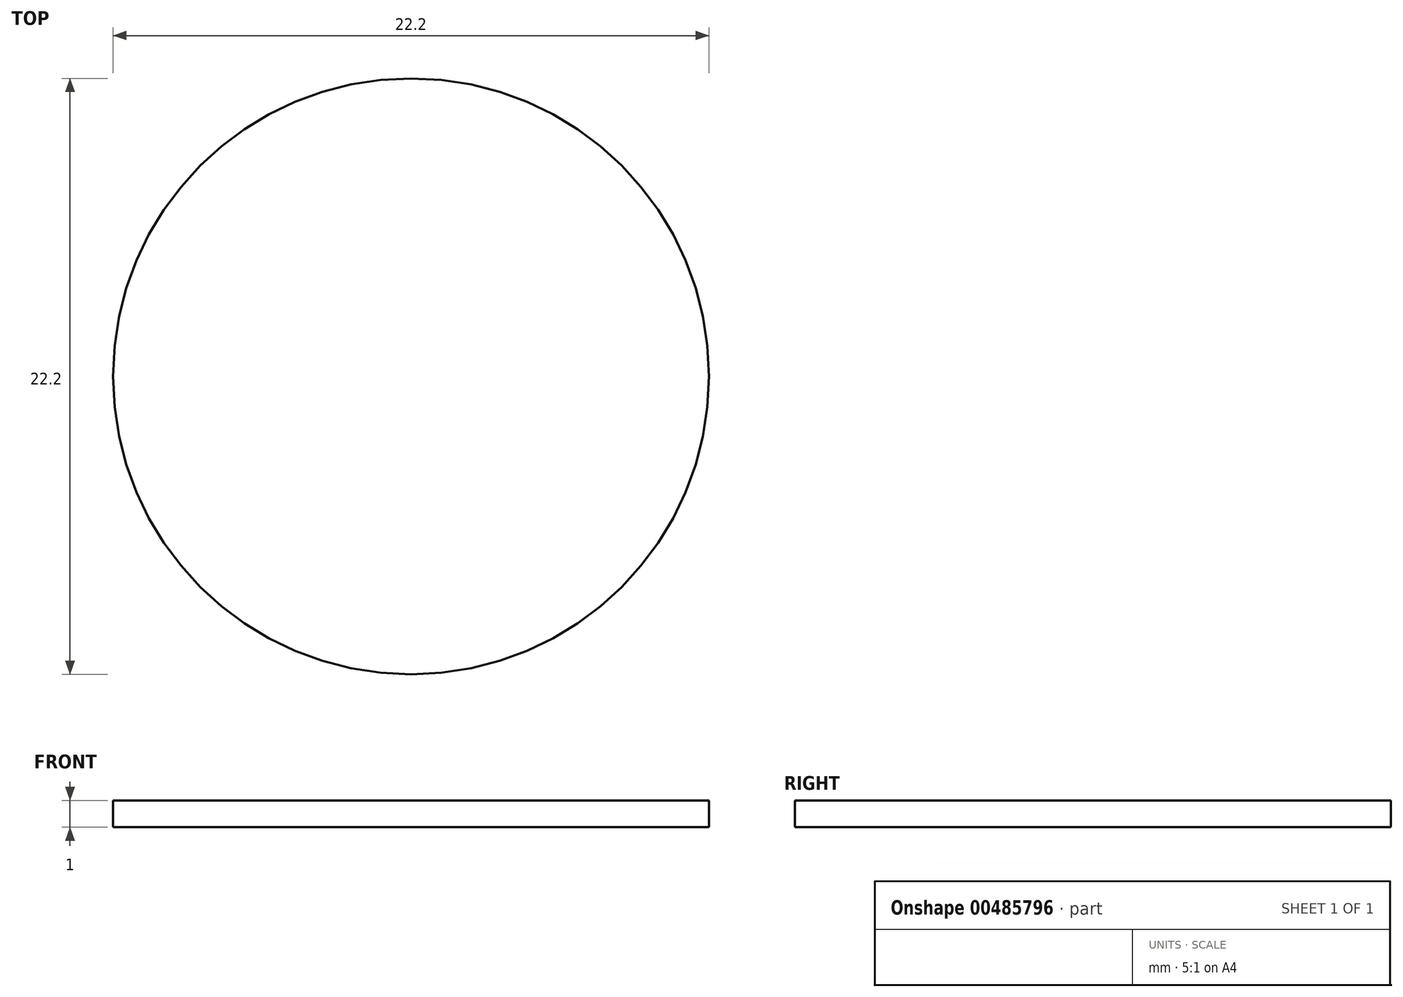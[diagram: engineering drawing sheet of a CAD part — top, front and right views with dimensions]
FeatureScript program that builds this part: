
annotation { "Feature Type Name" : "Feature", "Feature Type Description" : "" }
export const myFeature = defineFeature(function(context is Context, id is Id, definition is map)
    precondition{}
    {
        {
            var Q0;
            Q0=qCreatedBy(makeId("Top.planeOp"),FACE);
            var sketch = newSketch(context, id + "F0", { "sketchPlane" : qUnion([Q0])});
            skCircle(sketch, "E0", {"center": v(0, 0) * mm, "radius": 11.1 * mm});
            skSolve(sketch);
        }
        {
            var Q0;
            Q0 = qSketchRegion(id + "F0", true);
            extrude(context, id + "F1", {"entities" : qUnion([Q0]), "depth" : 1 * mm});
        }
    });
